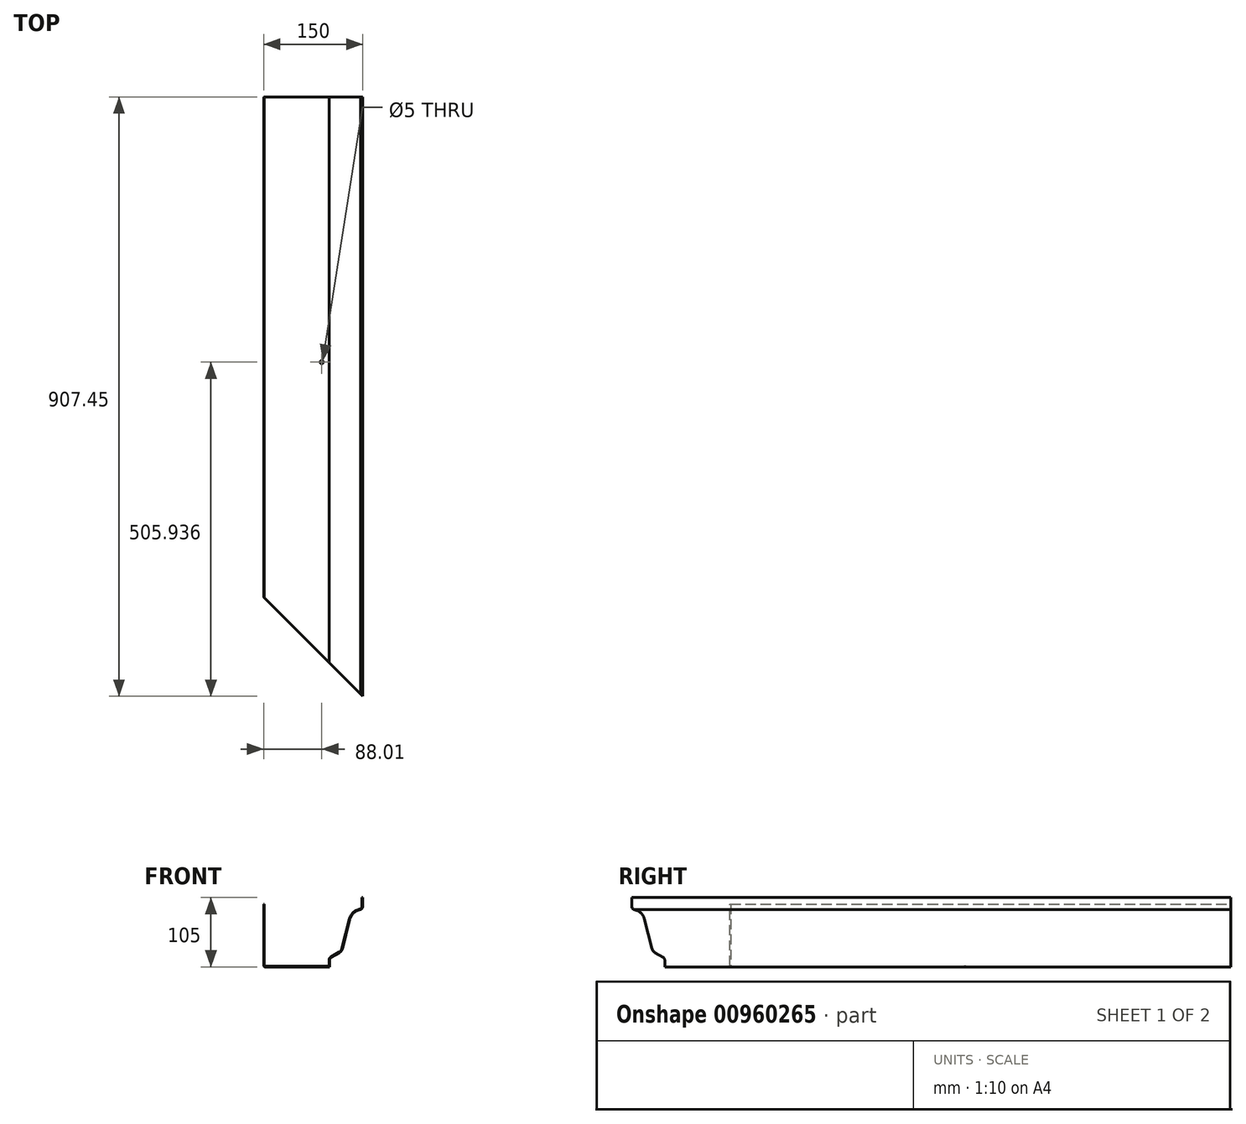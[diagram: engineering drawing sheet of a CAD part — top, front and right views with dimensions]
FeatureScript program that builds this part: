
annotation { "Feature Type Name" : "Feature", "Feature Type Description" : "" }
export const myFeature = defineFeature(function(context is Context, id is Id, definition is map)
    precondition{}
    {
        {
            var Q0;
            Q0=qCreatedBy(makeId("Front.planeOp"),FACE);
            var sketch = newSketch(context, id + "F0", { "sketchPlane" : qUnion([Q0])});
            skLineSegment(sketch, "E0.right", {"start": v(75, 52.5) * mm, "end": v(75, 38.91) * mm});
            skPoint(sketch, "E0.middle", {"position": v(0, 0) * mm});
            skArc(sketch, "E1", {"start": v(71.93, 34.26) * mm, "mid": v(61.54, 29.3) * mm, "end": v(55.61, 19.41) * mm});
            skArc(sketch, "E2", {"start": v(39.92, -30.84) * mm, "mid": v(42.75, -28.3) * mm, "end": v(44.39, -24.88) * mm});
            skArc(sketch, "E3", {"start": v(27.46, -38.2) * mm, "mid": v(25.66, -40.02) * mm, "end": v(25, -42.5) * mm});
            skLineSegment(sketch, "E4", {"start": v(27.46, -38.2) * mm, "end": v(39.92, -30.84) * mm});
            skLineSegment(sketch, "E5", {"start": v(44.39, -24.88) * mm, "end": v(55.61, 19.41) * mm});
            skArc(sketch, "E6", {"start": v(71.93, 34.26) * mm, "mid": v(74.17, 36.12) * mm, "end": v(75, 38.91) * mm});
            skPoint(sketch, "E7.orphan", {"position": v(-75, -52.5) * mm});
            skPoint(sketch, "E8.right.start.orphan", {"position": v(25, -52.5) * mm});
            skLineSegment(sketch, "E9", {"start": v(-73, -52.5) * mm, "end": v(25, -52.5) * mm});
            skLineSegment(sketch, "E10", {"start": v(25, -52.5) * mm, "end": v(25, -42.5) * mm});
            skLineSegment(sketch, "E11", {"start": v(-75, -50.5) * mm, "end": v(-75, 42.5) * mm});
            skLineSegment(sketch, "E12", {"start": v(-74, 42.5) * mm, "end": v(-74, -50.5) * mm});
            skLineSegment(sketch, "E13", {"start": v(-73, -51.5) * mm, "end": v(24, -51.5) * mm});
            skLineSegment(sketch, "E14", {"start": v(24, -51.5) * mm, "end": v(24, -42.5) * mm});
            skLineSegment(sketch, "E15", {"start": v(26.95, -37.33) * mm, "end": v(39.41, -29.98) * mm});
            skLineSegment(sketch, "E16", {"start": v(74, 52.5) * mm, "end": v(74, 38.88) * mm});
            skLineSegment(sketch, "E17", {"start": v(74, 52.5) * mm, "end": v(75, 52.5) * mm});
            skArc(sketch, "E18.trimOffspring", {"start": v(26.95, -37.33) * mm, "mid": v(24.79, -39.52) * mm, "end": v(24, -42.5) * mm});
            skArc(sketch, "E19", {"start": v(39.41, -29.98) * mm, "mid": v(41.95, -27.7) * mm, "end": v(43.42, -24.63) * mm});
            skArc(sketch, "E20", {"start": v(71.65, 35.23) * mm, "mid": v(60.82, 29.99) * mm, "end": v(54.64, 19.66) * mm});
            skLineSegment(sketch, "E21", {"start": v(54.64, 19.66) * mm, "end": v(43.42, -24.63) * mm});
            skArc(sketch, "E22", {"start": v(71.65, 35.23) * mm, "mid": v(73.36, 36.7) * mm, "end": v(74, 38.88) * mm});
            skPoint(sketch, "E23", {"position": v(-73, -50.5) * mm});
            skArc(sketch, "E24", {"start": v(-74, -50.5) * mm, "mid": v(-73.7, -51.2) * mm, "end": v(-73, -51.5) * mm});
            skArc(sketch, "E25", {"start": v(-75, -50.5) * mm, "mid": v(-74.41, -51.91) * mm, "end": v(-73, -52.5) * mm});
            skPoint(sketch, "E26.orphan", {"position": v(-74, -51.5) * mm});
            skLineSegment(sketch, "E27", {"start": v(-75, 42.5) * mm, "end": v(-74, 42.5) * mm});
            skSolve(sketch);
        }
        {
            var Q0;
            Q0=qSketchRegion(id+"F0",true);
            extrude(context, id + "F1", {"entities" : qUnion([Q0]), "depth" : 1000 * mm, "offsetDistance" : 25 * mm});
        }
        {
            var Q0;
            Q0=makeQuery(id+"F1.opExtrude","SWEPT_FACE",FACE,{"disambiguationData":[OSD([sQuery(id+"F0.wireOp",EDGE,"E9")])]});
            var sketch = newSketch(context, id + "F2", { "sketchPlane" : qUnion([Q0])});
            skLineSegment(sketch, "E28.left", {"start": v(-332.45, 532.75) * mm, "end": v(-332.45, 32.75) * mm});
            skLineSegment(sketch, "E29.right", {"start": v(167.55, 532.75) * mm, "end": v(167.55, 1032.75) * mm});
            skLineSegment(sketch, "E30", {"start": v(-332.45, 532.75) * mm, "end": v(167.55, 1032.75) * mm});
            skPoint(sketch, "E28.top.end.orphan", {"position": v(167.55, 32.75) * mm});
            skLineSegment(sketch, "E31.top", {"start": v(167.55, 32.75) * mm, "end": v(-332.45, 32.75) * mm});
            skLineSegment(sketch, "E31.left", {"start": v(167.55, 532.75) * mm, "end": v(167.55, 32.75) * mm});
            skPoint(sketch, "E32.end.orphan", {"position": v(167.55, 532.75) * mm});
            skCircle(sketch, "E33", {"center": v(13, 434.26) * mm, "radius": 2.5 * mm});
            skArc(sketch, "E34.trimOffspring", {"start": v(13, 434.26) * mm, "mid": v(13, 434.26) * mm, "end": v(13, 434.26) * mm});
            skArc(sketch, "E35.trimOffspring", {"start": v(13, 434.26) * mm, "mid": v(13, 434.27) * mm, "end": v(13, 434.27) * mm});
            skArc(sketch, "E36.trimOffspring", {"start": v(13, 434.27) * mm, "mid": v(13, 434.27) * mm, "end": v(13, 434.26) * mm});
            skSolve(sketch);
        }
        {
            var Q0;
            Q0 = qSketchRegion(id + "F2", true);
            extrude(context, id + "F3", {"entities" : qUnion([Q0]), "operationType" : NewBodyOperationType.INTERSECT, "oppositeDirection" : true, "depth" : 500 * mm, "offsetDistance" : 25 * mm});
        }
    });
